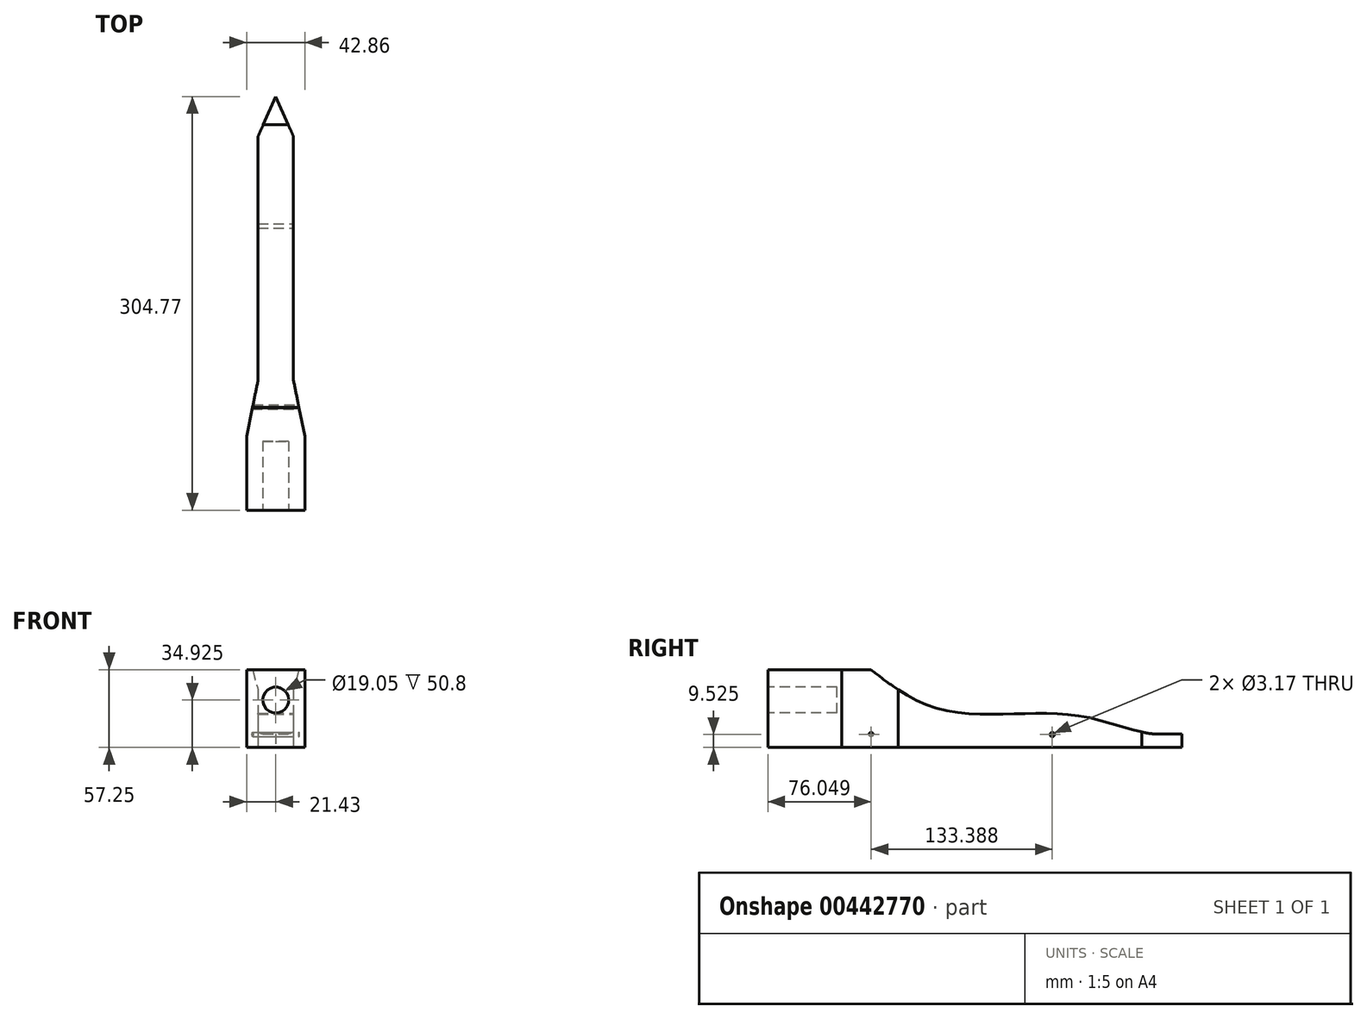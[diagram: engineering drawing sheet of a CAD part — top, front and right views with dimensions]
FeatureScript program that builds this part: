
annotation { "Feature Type Name" : "Feature", "Feature Type Description" : "" }
export const myFeature = defineFeature(function(context is Context, id is Id, definition is map)
    precondition{}
    {
        {
            var Q0;
            Q0=qCreatedBy(makeId("Right.planeOp"),FACE);
            var sketch = newSketch(context, id + "F0", { "sketchPlane" : qUnion([Q0])});
            skLineSegment(sketch, "E0", {"start": v(-152.4, 0) * mm, "end": v(152.4, 0) * mm});
            skLineSegment(sketch, "E1", {"start": v(-152.4, 0) * mm, "end": v(-152.4, 69.85) * mm});
            skLineSegment(sketch, "E2", {"start": v(152.4, 0) * mm, "end": v(152.4, 19.05) * mm});
            skLineSegment(sketch, "E3", {"start": v(152.4, 19.05) * mm, "end": v(-152.4, 69.85) * mm});
            skPoint(sketch, "E4.endSnap0", {"position": v(-152.4, 34.93) * mm});
            skLineSegment(sketch, "E5.0", {"start": v(-95.25, 50.8) * mm, "end": v(-152.4, 50.8) * mm, "construction": true});
            skLineSegment(sketch, "E5.1", {"start": v(-95.25, 50.8) * mm, "end": v(-95.25, 19.05) * mm, "construction": true});
            skLineSegment(sketch, "E5.2", {"start": v(-95.25, 19.05) * mm, "end": v(-152.4, 19.05) * mm, "construction": true});
            skSolve(sketch);
        }
        {
            var Q0;
            Q0=makeQuery(id+"F0.imprint","IMPRINT",FACE,{"disambiguationData":[TD([[makeQuery(id+"F0.imprint","IMPRINT",EDGE,{"derivedFrom":sQuery(id+"F0.wireOp",EDGE,"E0")}),1.0]])]});
            extrude(context, id + "F1", {"entities" : qUnion([Q0]), "depth" : 42.86 * mm, "symmetric" : true});
        }
        {
            var Q0;
            Q0=makeQuery(id+"F1.opExtrude","SWEPT_FACE",FACE,{"disambiguationData":[OSD([sQuery(id+"F0.wireOp",EDGE,"E1")])]});
            var sketch = newSketch(context, id + "F2", { "sketchPlane" : qUnion([Q0])});
            skLineSegment(sketch, "E6", {"start": v(21.43, 34.93) * mm, "end": v(0, 34.93) * mm, "construction": true});
            skCircle(sketch, "E7", {"center": v(0, 34.93) * mm, "radius": 9.53 * mm});
            skSolve(sketch);
        }
        {
            var Q0;
            Q0=makeQuery(id+"F2.imprint","IMPRINT",FACE,{"disambiguationData":[TD([[makeQuery(id+"F2.imprint","IMPRINT",EDGE,{"derivedFrom":sQuery(id+"F2.wireOp",EDGE,"E7")}),1.0]])]});
            var Q1;
            Q1=sQuery(id+"F2.wireOp",EDGE,"E7");
            extrude(context, id + "F3", {"entities" : qUnion([Q0]), "operationType" : NewBodyOperationType.REMOVE, "surfaceEntities" : qUnion([Q1]), "oppositeDirection" : true, "depth" : 50.8 * mm});
        }
        {
            var Q0;
            Q0=makeQuery(id+"F1.opExtrude","CAP_FACE",FACE,{"disambiguationData":[OSD([sQuery(id+"F0.wireOp",EDGE,"E0"),sQuery(id+"F0.wireOp",EDGE,"E1"),sQuery(id+"F0.wireOp",EDGE,"E2"),sQuery(id+"F0.wireOp",EDGE,"E3")])],"isStart":false});
            var sketch = newSketch(context, id + "F4", { "sketchPlane" : qUnion([Q0])});
            skLineSegment(sketch, "E8", {"start": v(-152.4, 34.93) * mm, "end": v(-152.4, 44.45) * mm, "construction": true});
            skLineSegment(sketch, "E9.0", {"start": v(-95.25, 19.05) * mm, "end": v(-152.4, 19.05) * mm, "construction": true});
            skLineSegment(sketch, "E9.1", {"start": v(-95.25, 50.8) * mm, "end": v(-95.25, 19.05) * mm, "construction": true});
            skLineSegment(sketch, "E9.2", {"start": v(-152.4, 50.8) * mm, "end": v(-95.25, 50.8) * mm, "construction": true});
            skLineSegment(sketch, "E10", {"start": v(57.15, 0) * mm, "end": v(57.15, 34.93) * mm, "construction": true});
            skLineSegment(sketch, "E11", {"start": v(-152.4, 44.45) * mm, "end": v(-101.6, 44.45) * mm, "construction": true});
            skLineSegment(sketch, "E12", {"start": v(-101.6, 44.45) * mm, "end": v(-101.6, 25.4) * mm, "construction": true});
            skLineSegment(sketch, "E13", {"start": v(-101.6, 25.4) * mm, "end": v(-152.4, 25.4) * mm, "construction": true});
            skSolve(sketch);
        }
        {
            var Q0;
            Q0=makeQuery(id+"F1.opExtrude","SWEPT_FACE",FACE,{"disambiguationData":[OSD([sQuery(id+"F0.wireOp",EDGE,"E0")])]});
            var sketch = newSketch(context, id + "F5", { "sketchPlane" : qUnion([Q0])});
            skLineSegment(sketch, "E14", {"start": v(0, 152.4) * mm, "end": v(0, -152.4) * mm, "construction": true});
            skLineSegment(sketch, "E15", {"start": v(21.43, -57.15) * mm, "end": v(-21.43, -57.15) * mm, "construction": true});
            skLineSegment(sketch, "E16", {"start": v(15.88, 152.4) * mm, "end": v(15.88, 95.25) * mm, "construction": true});
            skLineSegment(sketch, "E17", {"start": v(15.88, 95.25) * mm, "end": v(-15.87, 95.25) * mm, "construction": true});
            skLineSegment(sketch, "E18", {"start": v(-15.87, 95.25) * mm, "end": v(-15.87, 152.4) * mm, "construction": true});
            skLineSegment(sketch, "E19", {"start": v(0, 152.4) * mm, "end": v(-9.53, 152.4) * mm, "construction": true});
            skLineSegment(sketch, "E20", {"start": v(-9.53, 152.4) * mm, "end": v(-9.53, 101.6) * mm, "construction": true});
            skLineSegment(sketch, "E21", {"start": v(-9.52, 101.6) * mm, "end": v(9.53, 101.6) * mm, "construction": true});
            skLineSegment(sketch, "E22", {"start": v(9.53, 101.6) * mm, "end": v(9.53, 152.4) * mm, "construction": true});
            skSolve(sketch);
        }
        {
            var Q0;
            Q0=makeQuery(id+"F4.imprint","IMPRINT",FACE,{"disambiguationData":[TD([[makeQuery(id+"F4.imprint","IMPRINT",EDGE,{"derivedFrom":makeQuery(id+"F1.opExtrude","CAP_EDGE",EDGE,{"disambiguationData":[OSD([sQuery(id+"F0.wireOp",EDGE,"E0")])],"isStart":false})}),1.0]])]});
            var sketch = newSketch(context, id + "F6", { "sketchPlane" : qUnion([Q0])});
            skLineSegment(sketch, "E23", {"start": v(-152.4, 0) * mm, "end": v(152.4, 0) * mm});
            skLineSegment(sketch, "E24", {"start": v(152.4, 0) * mm, "end": v(152.4, 9.95) * mm});
            skLineSegment(sketch, "E25", {"start": v(-152.4, 57.25) * mm, "end": v(-152.4, 0) * mm});
            skPoint(sketch, "E26.orphan", {"position": v(-152.42, 0) * mm});
            skFitSpline(sketch, "E27", {"points": [v(-76.56, 57.25) * mm, v(-30.84, 29.7) * mm, v(27.16, 24.61) * mm, v(81.6, 22.42) * mm, v(131.55, 9.95) * mm, v(152.4, 13.3) * mm], "startDerivative": vector(200.51, -153.98) * mm, "endDerivative": vector(137.61, 45.32) * mm});
            skLineSegment(sketch, "E28", {"start": v(131.55, 9.95) * mm, "end": v(152.4, 9.95) * mm});
            skLineSegment(sketch, "E29", {"start": v(-76.56, 57.25) * mm, "end": v(-152.4, 57.25) * mm});
            skCircle(sketch, "E30", {"center": v(57.04, 9.53) * mm, "radius": 1.59 * mm});
            skCircle(sketch, "E31", {"center": v(-76.35, 9.53) * mm, "radius": 1.59 * mm});
            skSolve(sketch);
        }
        {
            var Q0;
            Q0 = qSketchRegion(id + "F6", true);
            extrude(context, id + "F7", {"entities" : qUnion([Q0]), "operationType" : NewBodyOperationType.INTERSECT, "endBound" : BoundingType.THROUGH_ALL, "oppositeDirection" : true, "depth" : 25.4 * mm});
        }
        {
            var Q0;
            {var subQ0=sQuery(id+"F0.wireOp",EDGE,"E0");Q0=makeQuery(id+"F5.imprint","IMPRINT",FACE,{"disambiguationData":[TD([[makeQuery(id+"F5.imprint","IMPRINT",EDGE,{"derivedFrom":makeQuery(id+"F1.opExtrude","CAP_EDGE",EDGE,{"disambiguationData":[OSD([subQ0])],"isStart":true})}),1.0]])]});}
            var sketch = newSketch(context, id + "F8", { "sketchPlane" : qUnion([Q0])});
            skLineSegment(sketch, "E32", {"start": v(-21.43, 152.4) * mm, "end": v(-21.43, 97.88) * mm});
            skPoint(sketch, "E33.end.orphan", {"position": v(0, -151.53) * mm});
            skLineSegment(sketch, "E34.MirrorCS", {"start": v(21.43, 152.4) * mm, "end": v(21.43, 74.56) * mm});
            skPoint(sketch, "E35.orphan", {"position": v(-21.43, 152.4) * mm});
            skPoint(sketch, "E36.orphan", {"position": v(21.43, 152.4) * mm});
            skLineSegment(sketch, "E37", {"start": v(-21.43, 152.4) * mm, "end": v(21.43, 152.4) * mm});
            skPoint(sketch, "E38.MirrorCS.end.orphan", {"position": v(21.35, -128.98) * mm});
            skPoint(sketch, "E38.MirrorCS.start.orphan", {"position": v(0, -152.37) * mm});
            skPoint(sketch, "E39.start.orphan", {"position": v(-21.35, -128.98) * mm});
            skLineSegment(sketch, "E40", {"start": v(13.03, 56.53) * mm, "end": v(13.03, -123.03) * mm});
            skLineSegment(sketch, "E41", {"start": v(13.03, -123.03) * mm, "end": v(0, -152.37) * mm});
            skPoint(sketch, "E42.MirrorCS.end.orphan", {"position": v(8.78, -125.71) * mm});
            skPoint(sketch, "E42.MirrorCS.start.orphan", {"position": v(8.78, 47.42) * mm});
            skLineSegment(sketch, "E43.MirrorCS", {"start": v(-13.03, 56.53) * mm, "end": v(-13.03, -123.03) * mm});
            skLineSegment(sketch, "E44.MirrorCS", {"start": v(-13.03, -123.03) * mm, "end": v(0, -152.37) * mm});
            skPoint(sketch, "E45.end.orphan", {"position": v(-8.78, -125.71) * mm});
            skPoint(sketch, "E46.orphan", {"position": v(-8.78, 47.42) * mm});
            skLineSegment(sketch, "E47", {"start": v(-21.43, 97.88) * mm, "end": v(-13.03, 56.53) * mm});
            skPoint(sketch, "E48.orphan", {"position": v(-21.43, 74.56) * mm});
            skLineSegment(sketch, "E49.MirrorCS", {"start": v(21.43, 97.88) * mm, "end": v(13.03, 56.53) * mm});
            skPoint(sketch, "E50.MirrorCS.start.orphan", {"position": v(21.43, 74.56) * mm});
            skSolve(sketch);
        }
        {
            var Q0;
            Q0 = qSketchRegion(id + "F8", true);
            extrude(context, id + "F9", {"entities" : qUnion([Q0]), "operationType" : NewBodyOperationType.INTERSECT, "endBound" : BoundingType.THROUGH_ALL, "oppositeDirection" : true, "depth" : 25.4 * mm});
        }
    });
